# Revit family: DC_Rheem_PLM_ HeavyDutyElectric_315L
name_source: partatom
category: Plumbing Fixtures
units: mm (PartAtom-declared; Revit-internal decimal feet)

## family parameters
Cut with Voids When Loaded = No
Host = Face
Part Type = Normal
Room Calculation Point = No
Round Connector Dimension = Use Radius
Shared = No

## types (6) — shared parameters
Cold Water Inlet Height = 128 mm  [stored 0.419948 ft]
Cold Water Pipe Radius = 1"
Dia = 638 mm  [stored 2.09318 ft]
H_ANZRS = 124 mm  [stored 0.406824 ft]
Height_ANZRS = 1635 mm  [stored 5.36417 ft]
HotWaterOutletHeight_ANZRS = 1294 mm
HotWaterPipeRadius_ANZRS = 1"
L1_ANZRS = 264 mm
Manufacturer = Rheem
Materials_ANZRS = Rheem - Joey Grey Steel
Radius_ANZRS = 319 mm  [stored 1.04659 ft]
T&PRValveConnection_ANZRS = 0"
URL = http://www.rheem.com.au
zero-valued in all types: Default Elevation

## per-type parameters (varying)
| type | Description | H1_ANZRS | Model | Type Comments |
| Heavy Duty Electric  - Indoor/Outdoor - 315L - 3 x 3.6kW | Heavy Duty Electric  - Indoor/Outdoor - 315L - 3 x 3.6kW | 475 mm | 61331507 | 500L first hour delivery @ 50oC rise |
| Heavy Duty Electric  - Indoor/Outdoor - 315L - 3 x 4.8kW | Heavy Duty Electric  - Indoor/Outdoor - 315L - 3 x 4.8kW | 475 mm | 61331508 | 560L first hour delivery @ 50oC rise |
| Heavy Duty Electric  - Indoor/Outdoor - 315L - 3 x 6.0kW | Heavy Duty Electric  - Indoor/Outdoor - 315L - 3 x 6.0kW | 475 mm | 61331509 | 620L first hour delivery @ 50oC rise |
| Heavy Duty Electric  - Indoor/Outdoor - 315L - 6 x 3.6kW | Heavy Duty Electric - Indoor/Outdoor - 315L - 6 x 3.6kW | 825 mm  [stored 2.70669 ft] | 61631507 | 690L first hour delivery @ 50oC rise |
| Heavy Duty Electric  - Indoor/Outdoor - 315L - 6 x 4.8kW | Heavy Duty Electric - Indoor/Outdoor - 315L - 6 x 4.8kW | 825 mm  [stored 2.70669 ft] | 61631508 | 810L first hour delivery @ 50oC rise |
| Heavy Duty Electric  - Indoor/Outdoor - 315L - 6 x 6.0kW | Heavy Duty Electric  - Indoor/Outdoor - 315L - 6 x 6.0kW | 825 mm  [stored 2.70669 ft] | 61631509 | 930L first hour delivery @ 50oC rise |

note: [stored X ft] marks values corroborated as IEEE doubles in the binary element streams (Revit-internal decimal feet)

## geometry (parser evidence)
native form markers: Blend x6, Sweep x2
no freeform markers — native parametric forms only
